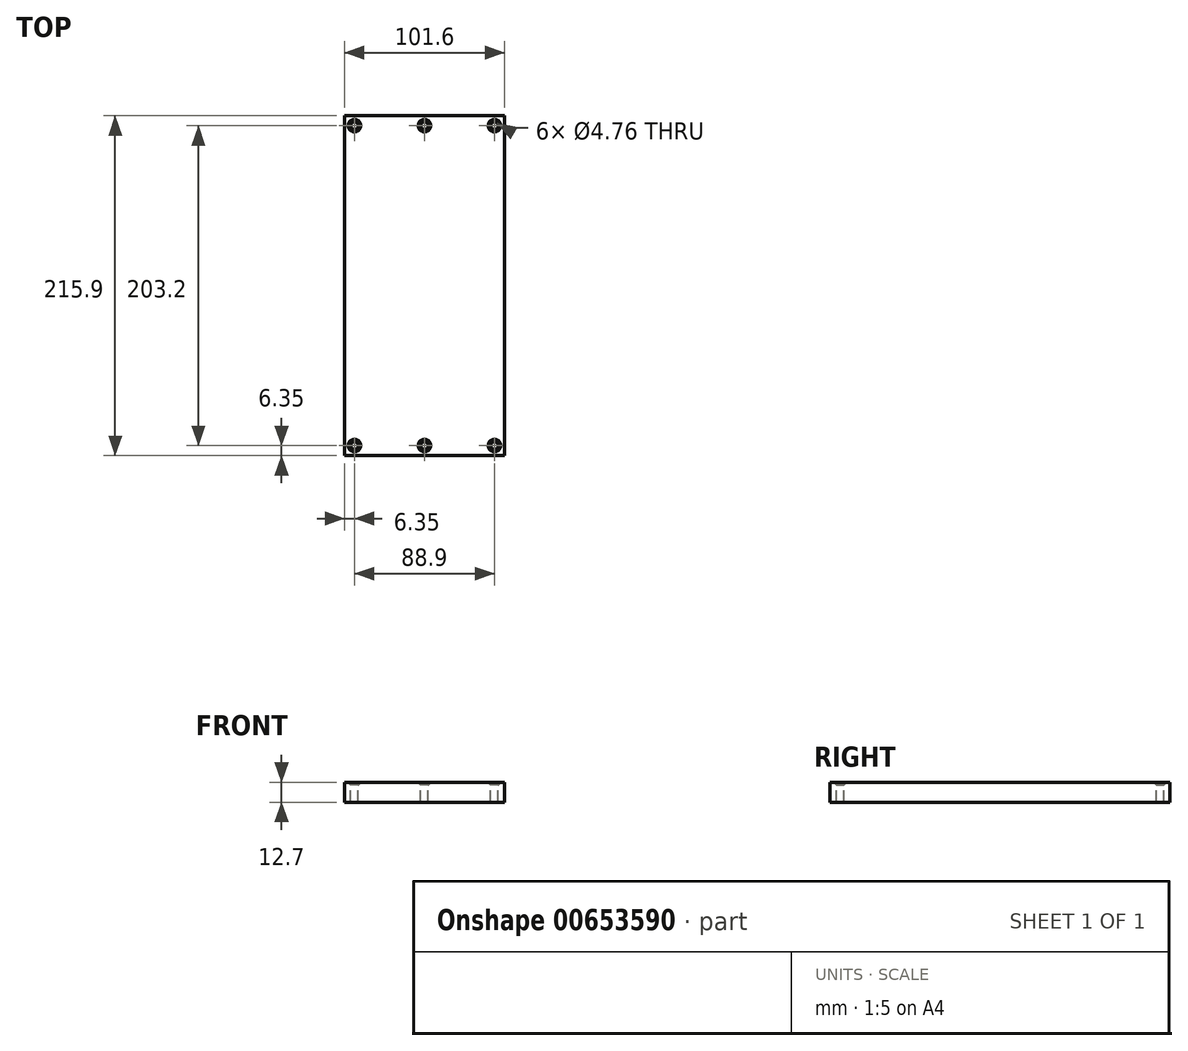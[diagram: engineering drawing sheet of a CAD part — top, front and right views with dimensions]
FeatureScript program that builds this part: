
annotation { "Feature Type Name" : "Feature", "Feature Type Description" : "" }
export const myFeature = defineFeature(function(context is Context, id is Id, definition is map)
    precondition{}
    {
        {
            var Q0;
            Q0=qCreatedBy(makeId("Top.planeOp"),FACE);
            var sketch = newSketch(context, id + "F0", { "sketchPlane" : qUnion([Q0])});
            skLineSegment(sketch, "E0.bottom", {"start": v(50.8, 107.95) * mm, "end": v(-50.8, 107.95) * mm});
            skLineSegment(sketch, "E0.top", {"start": v(50.8, -107.95) * mm, "end": v(-50.8, -107.95) * mm});
            skLineSegment(sketch, "E0.left", {"start": v(50.8, 107.95) * mm, "end": v(50.8, -107.95) * mm});
            skLineSegment(sketch, "E0.right", {"start": v(-50.8, 107.95) * mm, "end": v(-50.8, -107.95) * mm});
            skPoint(sketch, "E0.middle", {"position": v(0, 0) * mm});
            skSolve(sketch);
        }
        {
            var Q0;
            Q0=makeQuery(id+"F0.imprint","IMPRINT",FACE,{"disambiguationData":[TD([[makeQuery(id+"F0.imprint","IMPRINT",EDGE,{"derivedFrom":sQuery(id+"F0.wireOp",EDGE,"E0.bottom")}),1.0]])]});
            extrude(context, id + "F1", {"entities" : qUnion([Q0]), "depth" : 12.7 * mm, "offsetDistance" : 25.4 * mm});
        }
        {
            var Q0;
            Q0=makeQuery(id+"F1.opExtrude","CAP_FACE",FACE,{"disambiguationData":[OSD([sQuery(id+"F0.wireOp",EDGE,"E0.bottom"),sQuery(id+"F0.wireOp",EDGE,"E0.top"),sQuery(id+"F0.wireOp",EDGE,"E0.left"),sQuery(id+"F0.wireOp",EDGE,"E0.right")])],"isStart":false});
            var sketch = newSketch(context, id + "F2", { "sketchPlane" : qUnion([Q0])});
            skLineSegment(sketch, "E1.0", {"start": v(-44.45, -101.6) * mm, "end": v(44.45, -101.6) * mm});
            skLineSegment(sketch, "E1.1", {"start": v(-44.45, 101.6) * mm, "end": v(-44.45, -101.6) * mm});
            skLineSegment(sketch, "E1.2", {"start": v(44.45, 101.6) * mm, "end": v(-44.45, 101.6) * mm});
            skLineSegment(sketch, "E1.3", {"start": v(44.45, -101.6) * mm, "end": v(44.45, 101.6) * mm});
            skLineSegment(sketch, "E2", {"start": v(-44.45, -88.9) * mm, "end": v(44.45, -88.9) * mm});
            skLineSegment(sketch, "E3", {"start": v(44.45, 88.9) * mm, "end": v(-44.45, 88.9) * mm});
            skLineSegment(sketch, "E4", {"start": v(76.94, 0) * mm, "end": v(-80.05, 0) * mm, "construction": true});
            skPoint(sketch, "E5", {"position": v(0, 101.6) * mm});
            skPoint(sketch, "E6", {"position": v(14.82, 88.9) * mm});
            skPoint(sketch, "E7", {"position": v(-14.82, 88.9) * mm});
            skPoint(sketch, "E8", {"position": v(0, -101.6) * mm});
            skPoint(sketch, "E9", {"position": v(14.82, -88.9) * mm});
            skPoint(sketch, "E10", {"position": v(-14.82, -88.9) * mm});
            skLineSegment(sketch, "E11", {"start": v(-44.45, 88.9) * mm, "end": v(-14.82, 88.9) * mm, "construction": true});
            skLineSegment(sketch, "E12", {"start": v(-14.82, 88.9) * mm, "end": v(14.82, 88.9) * mm, "construction": true});
            skLineSegment(sketch, "E13", {"start": v(14.82, 88.9) * mm, "end": v(44.45, 88.9) * mm, "construction": true});
            skSolve(sketch);
        }
        {
            var Q0;
            Q0=sQuery(id+"F2.wireOp",VERTEX,"E5");
            var Q1;
            Q1=sQuery(id+"F2.wireOp",VERTEX,"E1.2.start");
            var Q2;
            Q2=sQuery(id+"F2.wireOp",VERTEX,"E1.2.end");
            var Q3;
            Q3=sQuery(id+"F2.wireOp",VERTEX,"E8");
            var Q4;
            Q4=sQuery(id+"F2.wireOp",VERTEX,"E1.3.start");
            var Q5;
            Q5=sQuery(id+"F2.wireOp",VERTEX,"E1.1.end");
            var Q6;
            Q6=makeQuery(id+"F1.opExtrude","SWEPT_BODY",BODY,{"disambiguationData":[OSD([sQuery(id+"F0.wireOp",EDGE,"E0.bottom"),sQuery(id+"F0.wireOp",EDGE,"E0.top"),sQuery(id+"F0.wireOp",EDGE,"E0.left"),sQuery(id+"F0.wireOp",EDGE,"E0.right")])]});
            hole(context, id + "F3", {"style" : HoleStyle.C_SINK, "endStyle" : HoleEndStyle.THROUGH, "holeDiameter" : 4.76 * mm, "cSinkDiameter" : 7.94 * mm, "cSinkAngle" : 85 * degree, "majorDiameter" : 6.35 * mm, "isTappedThrough" : true, "tappedDepth" : 12.7 * mm, "tapClearance" : 3, "locations" : qUnion([Q0, Q1, Q2, Q3, Q4, Q5]), "scope" : qUnion([Q6])});
        }
    });
